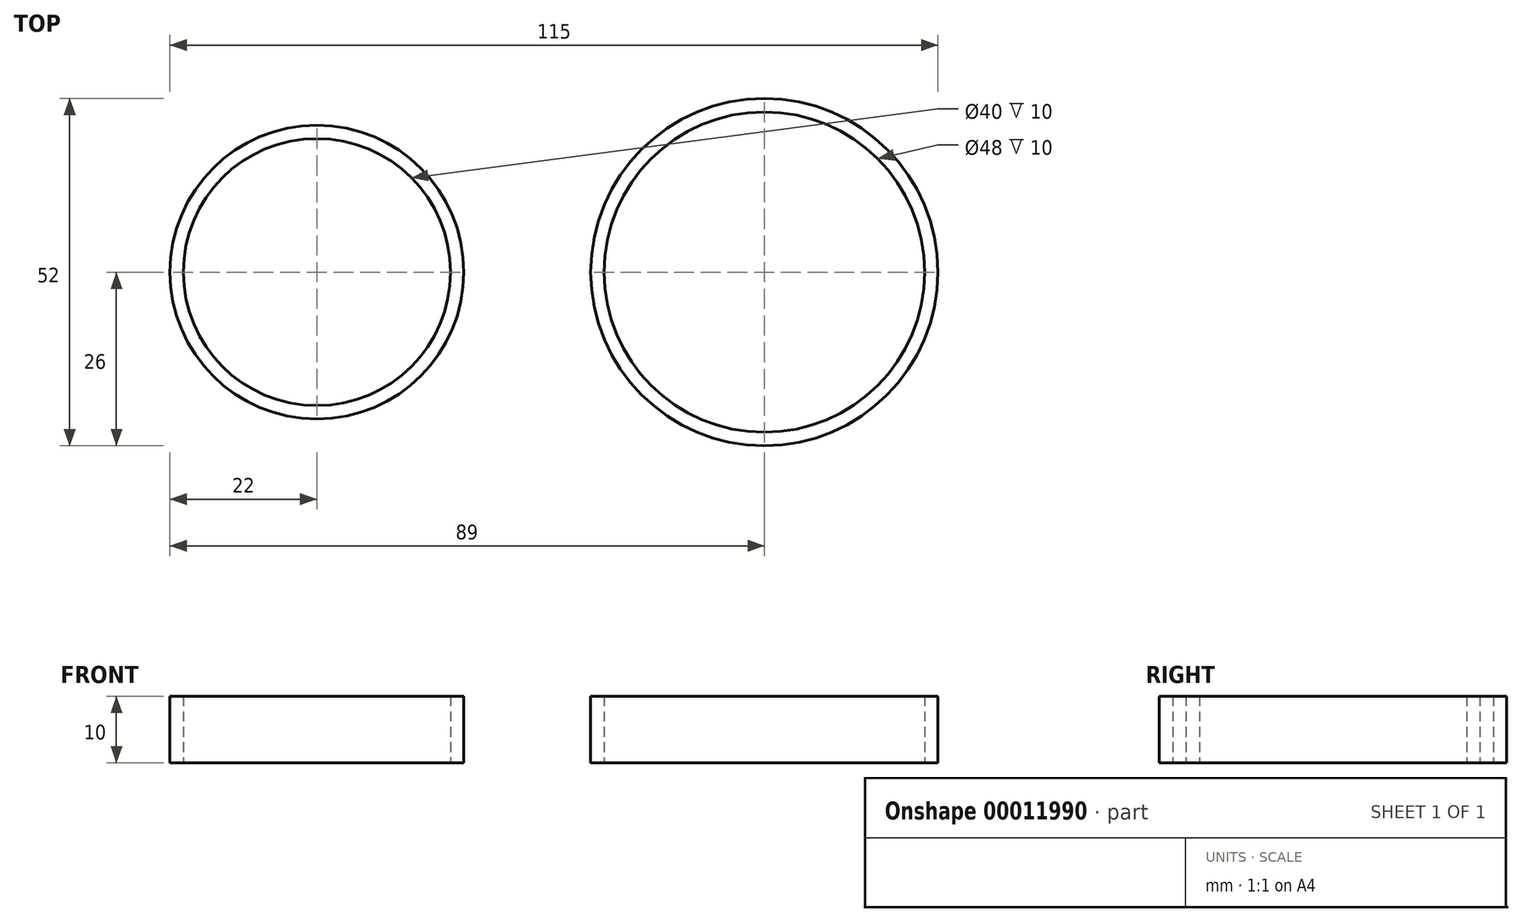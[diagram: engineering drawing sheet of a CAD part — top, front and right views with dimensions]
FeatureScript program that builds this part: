
annotation { "Feature Type Name" : "Feature", "Feature Type Description" : "" }
export const myFeature = defineFeature(function(context is Context, id is Id, definition is map)
    precondition{}
    {
        {
            var Q0;
            Q0=qCreatedBy(makeId("Top.planeOp"),FACE);
            var sketch = newSketch(context, id + "F0", { "sketchPlane" : qUnion([Q0])});
            skCircle(sketch, "E0", {"center": v(0, 0) * mm, "radius": 22 * mm});
            skCircle(sketch, "E1.0", {"center": v(0, 0) * mm, "radius": 20 * mm});
            skCircle(sketch, "E2", {"center": v(67, 0) * mm, "radius": 26 * mm});
            skCircle(sketch, "E3.0", {"center": v(67, 0) * mm, "radius": 24 * mm});
            skLineSegment(sketch, "E4", {"start": v(0, 0) * mm, "end": v(67, 0) * mm});
            skSolve(sketch);
        }
        {
            var Q0;
            Q0=makeQuery(id+"F0.imprint","IMPRINT",FACE,{"disambiguationData":[TD([[makeQuery(id+"F0.imprint","IMPRINT",EDGE,{"derivedFrom":sQuery(id+"F0.wireOp",EDGE,"E0")}),1.0]])]});
            var Q1;
            Q1=makeQuery(id+"F0.imprint","IMPRINT",FACE,{"disambiguationData":[TD([[makeQuery(id+"F0.imprint","IMPRINT",EDGE,{"derivedFrom":sQuery(id+"F0.wireOp",EDGE,"E2")}),1.0]])]});
            extrude(context, id + "F1", {"entities" : qUnion([Q0, Q1]), "depth" : 10 * mm});
        }
    });
